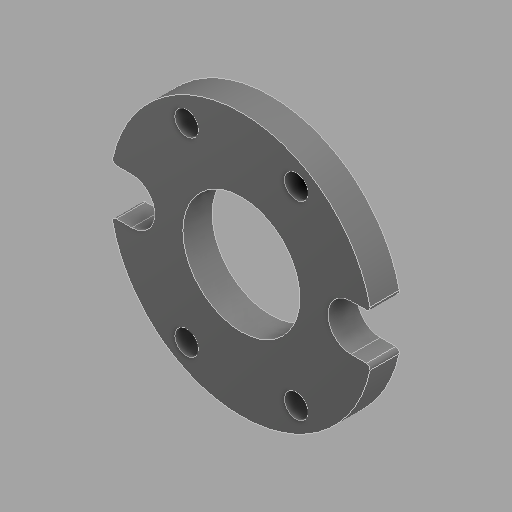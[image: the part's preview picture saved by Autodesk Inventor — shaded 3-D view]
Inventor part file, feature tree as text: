
AUTODESK INVENTOR PART (.ipt)
format: ipt  version: 2024.2 (Build 282272000, 272)  size: 123,392 bytes
history: native  units: in
note: dims shown in document units (in); Inventor stores cm internally (conversion verified against a paired STEP export)
features: fillet x1
ambient origin geometry x8: Origin, YZ Plane, XZ Plane, XY Plane, X Axis, Y Axis, Z Axis, Center Point
bodies: Solid1 (feature_tree)
feature tree (1):
  fillet  "Fillet1"  [1 undecoded]
note: 1 required parameter value undecoded (feature->parameter linkage not recoverable at this tier; creation-order binding heuristic only, values carry confidence <= 0.55)
